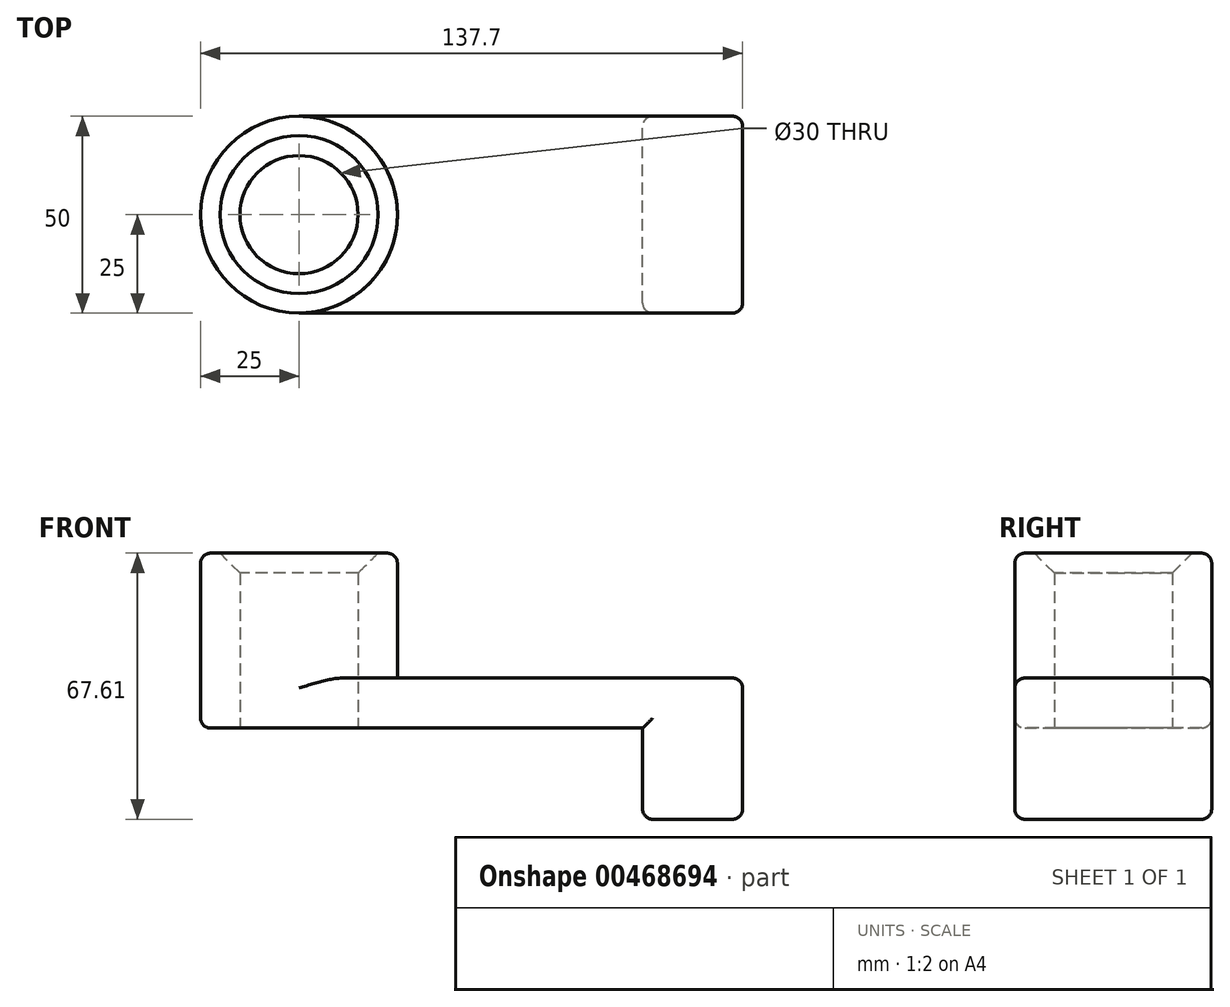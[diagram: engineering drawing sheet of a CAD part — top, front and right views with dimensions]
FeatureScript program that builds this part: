
annotation { "Feature Type Name" : "Feature", "Feature Type Description" : "" }
export const myFeature = defineFeature(function(context is Context, id is Id, definition is map)
    precondition{}
    {
        {
            var Q0;
            Q0=qCreatedBy(makeId("Top.planeOp"),FACE);
            var sketch = newSketch(context, id + "F0", { "sketchPlane" : qUnion([Q0])});
            skLineSegment(sketch, "E0.bottom", {"start": v(-50, 25) * mm, "end": v(50, 25) * mm});
            skLineSegment(sketch, "E0.top", {"start": v(-50, -25) * mm, "end": v(50, -25) * mm});
            skLineSegment(sketch, "E0.left", {"start": v(-50, 25) * mm, "end": v(-50, -25) * mm});
            skLineSegment(sketch, "E0.right", {"start": v(50, 25) * mm, "end": v(50, -25) * mm});
            skPoint(sketch, "E0.middle", {"position": v(0, 0) * mm});
            skCircle(sketch, "E1", {"center": v(-50, 0) * mm, "radius": 25 * mm});
            skCircle(sketch, "E2", {"center": v(-50, 0) * mm, "radius": 15 * mm});
            skSolve(sketch);
        }
        {
            var Q0;
            Q0 = qSketchRegion(id + "F0", true);
            extrude(context, id + "F1", {"entities" : qUnion([Q0]), "depth" : 12.7 * mm});
        }
        {
            var Q0;
            {var subQ1=sQuery(id+"F0.wireOp",EDGE,"E0.left");var subQ3=sQuery(id+"F0.wireOp",EDGE,"E2");var subQ4=makeQuery(id+"F0.imprint","INTERSECT",VERTEX,{"disambiguationData":[OD(0.0)],"derivedFrom":[subQ1,subQ3]});Q0=makeQuery(id+"F0.imprint","IMPRINT",FACE,{"disambiguationData":[TD([[makeQuery(id+"F0.imprint","IMPRINT",EDGE,{"disambiguationData":[TD([[subQ4,-1.0]])],"derivedFrom":subQ3}),-1.0]])]});}
            var Q1;
            {var subQ1=sQuery(id+"F0.wireOp",EDGE,"E0.left");var subQ3=sQuery(id+"F0.wireOp",EDGE,"E2");var subQ4=makeQuery(id+"F0.imprint","INTERSECT",VERTEX,{"disambiguationData":[OD(0.0)],"derivedFrom":[subQ1,subQ3]});Q1=makeQuery(id+"F0.imprint","IMPRINT",FACE,{"disambiguationData":[TD([[makeQuery(id+"F0.imprint","IMPRINT",EDGE,{"disambiguationData":[TD([[subQ4,1.0]])],"derivedFrom":subQ3}),-1.0]])]});}
            extrude(context, id + "F2", {"entities" : qUnion([Q0, Q1]), "operationType" : NewBodyOperationType.ADD, "depth" : 44.45 * mm});
        }
        {
            var Q0;
            Q0=makeQuery(id+"F1.opExtrude","SWEPT_FACE",FACE,{"disambiguationData":[OSD([sQuery(id+"F0.wireOp",EDGE,"E0.right")])]});
            var sketch = newSketch(context, id + "F3", { "sketchPlane" : qUnion([Q0])});
            skLineSegment(sketch, "E3.bottom", {"start": v(-25, 12.7) * mm, "end": v(25, 12.7) * mm});
            skLineSegment(sketch, "E3.top", {"start": v(-25, -23.16) * mm, "end": v(25, -23.16) * mm});
            skLineSegment(sketch, "E3.left", {"start": v(-25, 12.7) * mm, "end": v(-25, -23.16) * mm});
            skLineSegment(sketch, "E3.right", {"start": v(25, 12.7) * mm, "end": v(25, -23.16) * mm});
            skLineSegment(sketch, "E4.bottom", {"start": v(0, 0) * mm, "end": v(0, 0) * mm});
            skLineSegment(sketch, "E4.top", {"start": v(0, -23.16) * mm, "end": v(0, -23.16) * mm});
            skLineSegment(sketch, "E4.left", {"start": v(0, 0) * mm, "end": v(0, -23.16) * mm, "construction": true});
            skLineSegment(sketch, "E4.right", {"start": v(0, 0) * mm, "end": v(0, -23.16) * mm, "construction": true});
            skCircle(sketch, "E5", {"center": v(-12.27, -12) * mm, "radius": 5.42 * mm, "construction": true});
            skCircle(sketch, "E6.MirrorC", {"center": v(12.27, -12) * mm, "radius": 5.42 * mm, "construction": true});
            skCircle(sketch, "E7", {"center": v(-12.27, -12) * mm, "radius": 2.33 * mm, "construction": true});
            skCircle(sketch, "E8", {"center": v(6.08, 113.63) * mm, "radius": 2.03 * mm, "construction": true});
            skCircle(sketch, "E9", {"center": v(12.27, -12) * mm, "radius": 2.22 * mm, "construction": true});
            skSolve(sketch);
        }
        {
            var Q0;
            Q0 = qSketchRegion(id + "F3", true);
            extrude(context, id + "F4", {"entities" : qUnion([Q0]), "operationType" : NewBodyOperationType.ADD, "endBound" : BoundingType.SYMMETRIC, "depth" : 25.4 * mm});
        }
        {
            var Q0;
            Q0=makeQuery(id+"F4.boolean.opBoolean","MERGE",EDGE,{"derivedFrom":[makeQuery(id+"F1.opExtrude","CAP_EDGE",EDGE,{"disambiguationData":[OSD([sQuery(id+"F0.wireOp",EDGE,"E0.top")])],"isStart":false}),makeQuery(id+"F4.opExtrude","SWEPT_EDGE",EDGE,{"disambiguationData":[OSD([sQuery(id+"F3.wireOp",EDGE,"E3.bottom"),sQuery(id+"F3.wireOp",EDGE,"E3.left")])]})]});
            var Q1;
            Q1=makeQuery(id+"F4.boolean.opBoolean","MERGE",EDGE,{"derivedFrom":[makeQuery(id+"F1.opExtrude","CAP_EDGE",EDGE,{"disambiguationData":[OSD([sQuery(id+"F0.wireOp",EDGE,"E0.bottom")])],"isStart":false}),makeQuery(id+"F4.opExtrude","SWEPT_EDGE",EDGE,{"disambiguationData":[OSD([sQuery(id+"F3.wireOp",EDGE,"E3.bottom"),sQuery(id+"F3.wireOp",EDGE,"E3.right")])]})]});
            var Q2;
            Q2=makeQuery(id+"F4.opExtrude","CAP_EDGE",EDGE,{"disambiguationData":[OSD([sQuery(id+"F3.wireOp",EDGE,"E3.bottom")])],"isStart":false});
            var Q3;
            Q3=makeQuery(id+"F4.opExtrude","CAP_EDGE",EDGE,{"disambiguationData":[OSD([sQuery(id+"F3.wireOp",EDGE,"E3.top")])],"isStart":false});
            var Q4;
            Q4=makeQuery(id+"F1.opExtrude","CAP_EDGE",EDGE,{"disambiguationData":[OSD([sQuery(id+"F0.wireOp",EDGE,"E0.top")])],"isStart":true});
            var Q5;
            Q5=makeQuery(id+"F4.opExtrude","CAP_EDGE",EDGE,{"disambiguationData":[OSD([sQuery(id+"F3.wireOp",EDGE,"E3.left")])],"isStart":true});
            var Q6;
            Q6=makeQuery(id+"F4.opExtrude","SWEPT_EDGE",EDGE,{"disambiguationData":[OSD([sQuery(id+"F3.wireOp",EDGE,"E3.top"),sQuery(id+"F3.wireOp",EDGE,"E3.left")])]});
            var Q7;
            Q7=makeQuery(id+"F4.opExtrude","CAP_EDGE",EDGE,{"disambiguationData":[OSD([sQuery(id+"F3.wireOp",EDGE,"E3.left")])],"isStart":false});
            var Q8;
            Q8=makeQuery(id+"F4.opExtrude","CAP_EDGE",EDGE,{"disambiguationData":[OSD([sQuery(id+"F3.wireOp",EDGE,"E3.right")])],"isStart":false});
            var Q9;
            Q9=makeQuery(id+"F4.opExtrude","SWEPT_EDGE",EDGE,{"disambiguationData":[OSD([sQuery(id+"F3.wireOp",EDGE,"E3.top"),sQuery(id+"F3.wireOp",EDGE,"E3.right")])]});
            var Q10;
            Q10=makeQuery(id+"F4.opExtrude","CAP_EDGE",EDGE,{"disambiguationData":[OSD([sQuery(id+"F3.wireOp",EDGE,"E3.right")])],"isStart":true});
            var Q11;
            Q11=makeQuery(id+"F4.opExtrude","CAP_EDGE",EDGE,{"disambiguationData":[OSD([sQuery(id+"F3.wireOp",EDGE,"E3.top")])],"isStart":true});
            var Q12;
            Q12=makeQuery(id+"F2.opExtrude","CAP_EDGE",EDGE,{"disambiguationData":[OSD([sQuery(id+"F0.wireOp",EDGE,"E1")])],"isStart":false});
            fillet(context, id + "F5", {"entities" : qUnion([Q0, Q1, Q2, Q3, Q4, Q5, Q6, Q7, Q8, Q9, Q10, Q11, Q12]), "radius" : 2.54 * mm, "tangentPropagation" : true, "allowEdgeOverflow" : false});
        }
        {
            var Q0;
            Q0=makeQuery(id+"F2.opExtrude","CAP_EDGE",EDGE,{"disambiguationData":[OSD([sQuery(id+"F0.wireOp",EDGE,"E2")])],"isStart":false});
            chamfer(context, id + "F6", {"entities" : qUnion([Q0]), "width" : 5.08 * mm, "tangentPropagation" : true});
        }
    });
